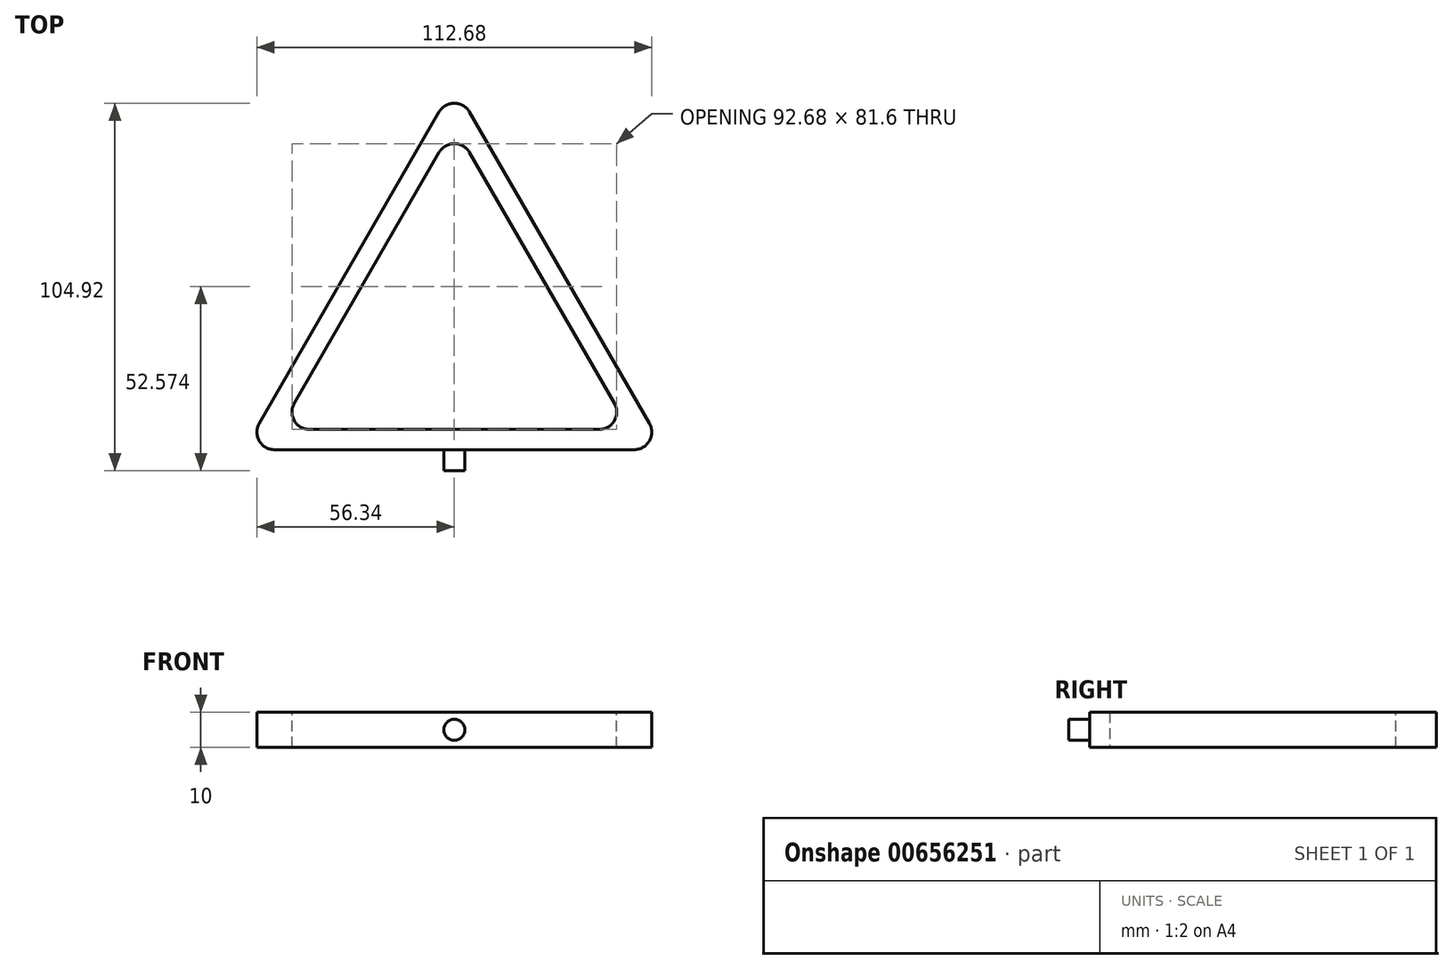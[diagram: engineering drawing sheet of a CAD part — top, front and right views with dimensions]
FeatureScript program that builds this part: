
annotation { "Feature Type Name" : "Feature", "Feature Type Description" : "" }
export const myFeature = defineFeature(function(context is Context, id is Id, definition is map)
    precondition{}
    {
        {
            var Q0;
            Q0=qCreatedBy(makeId("Top.planeOp"),FACE);
            var sketch = newSketch(context, id + "F0", { "sketchPlane" : qUnion([Q0])});
            skCircle(sketch, "E0.cCircle", {"center": v(0, 0) * mm, "radius": 34.64 * mm, "construction": true});
            skLineSegment(sketch, "E0.0", {"start": v(0, 69.28) * mm, "end": v(60, -34.64) * mm});
            skLineSegment(sketch, "E0.1", {"start": v(60, -34.64) * mm, "end": v(-60, -34.64) * mm});
            skLineSegment(sketch, "E0.2", {"start": v(-60, -34.64) * mm, "end": v(0, 69.28) * mm});
            skPoint(sketch, "E0.0.midPoint", {"position": v(30, 17.32) * mm});
            skCircle(sketch, "E1.cCircle", {"center": v(0, 0) * mm, "radius": 28.87 * mm, "construction": true});
            skLineSegment(sketch, "E1.0", {"start": v(50, -28.87) * mm, "end": v(-50, -28.87) * mm});
            skLineSegment(sketch, "E1.1", {"start": v(-50, -28.87) * mm, "end": v(0, 57.74) * mm});
            skLineSegment(sketch, "E1.2", {"start": v(0, 57.74) * mm, "end": v(50, -28.87) * mm});
            skPoint(sketch, "E1.0.midPoint", {"position": v(0, -28.87) * mm});
            skSolve(sketch);
        }
        {
            var Q0;
            Q0 = qSketchRegion(id + "F0", true);
            extrude(context, id + "F1", {"entities" : qUnion([Q0]), "depth" : 10 * mm, "offsetDistance" : 25 * mm});
        }
        {
            var Q0;
            Q0=makeQuery(id+"F1.opExtrude","SWEPT_EDGE",EDGE,{"disambiguationData":[OSD([sQuery(id+"F0.wireOp",EDGE,"E0.1"),sQuery(id+"F0.wireOp",EDGE,"E0.2")])]});
            var Q1;
            Q1=makeQuery(id+"F1.opExtrude","SWEPT_EDGE",EDGE,{"disambiguationData":[OSD([sQuery(id+"F0.wireOp",EDGE,"E0.0"),sQuery(id+"F0.wireOp",EDGE,"E0.1")])]});
            var Q2;
            Q2=makeQuery(id+"F1.opExtrude","SWEPT_EDGE",EDGE,{"disambiguationData":[OSD([sQuery(id+"F0.wireOp",EDGE,"E0.0"),sQuery(id+"F0.wireOp",EDGE,"E0.2")])]});
            var Q3;
            Q3=makeQuery(id+"F1.opExtrude","SWEPT_EDGE",EDGE,{"disambiguationData":[OSD([sQuery(id+"F0.wireOp",EDGE,"E1.0"),sQuery(id+"F0.wireOp",EDGE,"E1.2")])]});
            var Q4;
            Q4=makeQuery(id+"F1.opExtrude","SWEPT_EDGE",EDGE,{"disambiguationData":[OSD([sQuery(id+"F0.wireOp",EDGE,"E1.1"),sQuery(id+"F0.wireOp",EDGE,"E1.2")])]});
            var Q5;
            Q5=makeQuery(id+"F1.opExtrude","SWEPT_EDGE",EDGE,{"disambiguationData":[OSD([sQuery(id+"F0.wireOp",EDGE,"E1.0"),sQuery(id+"F0.wireOp",EDGE,"E1.1")])]});
            fillet(context, id + "F2", {"entities" : qUnion([Q0, Q1, Q2, Q3, Q4, Q5]), "radius" : 5 * mm, "tangentPropagation" : true, "allowEdgeOverflow" : false});
        }
        {
            var Q0;
            Q0=makeQuery(id+"F1.opExtrude","SWEPT_FACE",FACE,{"disambiguationData":[OSD([sQuery(id+"F0.wireOp",EDGE,"E0.1")])]});
            var sketch = newSketch(context, id + "F3", { "sketchPlane" : qUnion([Q0])});
            skCircle(sketch, "E2", {"center": v(0, 5) * mm, "radius": 3 * mm});
            skSolve(sketch);
        }
        {
            var Q0;
            Q0 = qSketchRegion(id + "F3", true);
            extrude(context, id + "F4", {"entities" : qUnion([Q0]), "operationType" : NewBodyOperationType.ADD, "depth" : 6 * mm, "offsetDistance" : 25 * mm});
        }
    });
